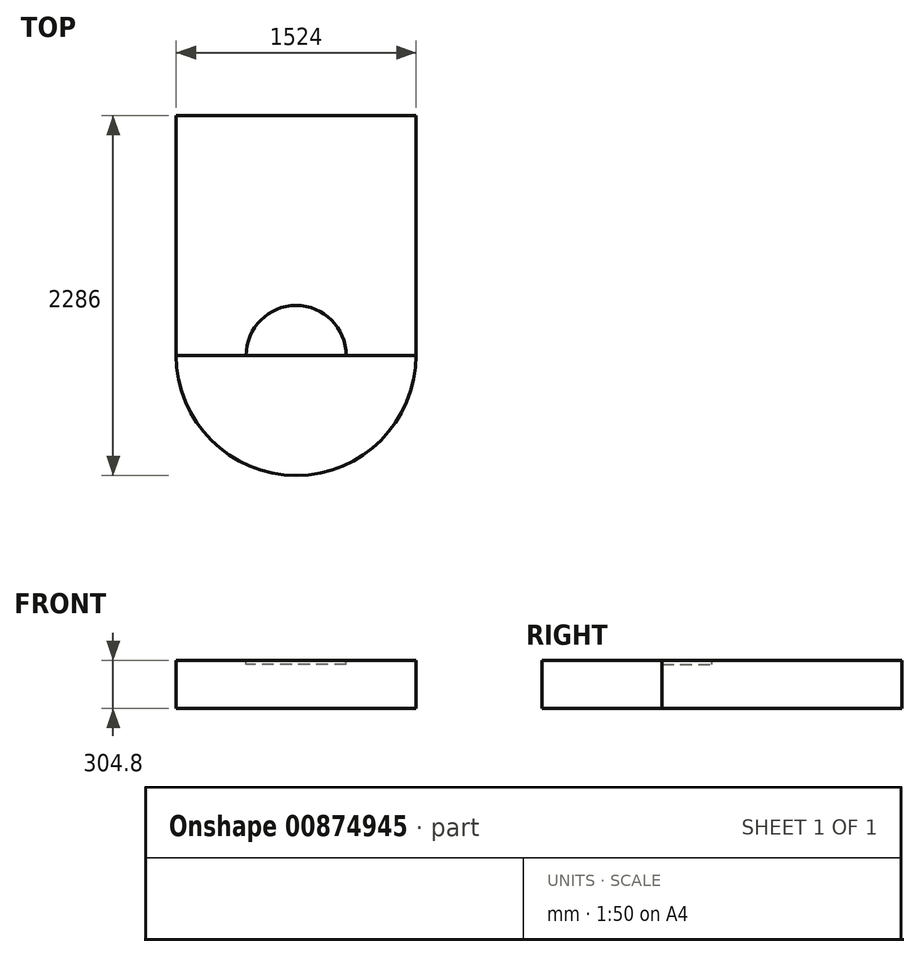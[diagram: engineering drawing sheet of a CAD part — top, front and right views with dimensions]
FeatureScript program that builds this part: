
annotation { "Feature Type Name" : "Feature", "Feature Type Description" : "" }
export const myFeature = defineFeature(function(context is Context, id is Id, definition is map)
    precondition{}
    {
        {
            var Q0;
            Q0=qCreatedBy(makeId("Top.planeOp"),FACE);
            var sketch = newSketch(context, id + "F0", { "sketchPlane" : qUnion([Q0])});
            skLineSegment(sketch, "E0", {"start": v(0, 0) * mm, "end": v(1524, 0) * mm});
            skLineSegment(sketch, "E1", {"start": v(1524, 0) * mm, "end": v(1524, -1524) * mm});
            skLineSegment(sketch, "E2", {"start": v(1524, -1524) * mm, "end": v(0, -1524) * mm});
            skLineSegment(sketch, "E3", {"start": v(0, -1524) * mm, "end": v(0, 0) * mm});
            skSolve(sketch);
        }
        {
            var Q0;
            Q0=makeQuery(id+"F0.imprint","IMPRINT",FACE,{"disambiguationData":[TD([[makeQuery(id+"F0.imprint","IMPRINT",EDGE,{"derivedFrom":sQuery(id+"F0.wireOp",EDGE,"E0")}),-1.0]])]});
            extrude(context, id + "F1", {"entities" : qUnion([Q0]), "depth" : 304.8 * mm, "offsetDistance" : 25.4 * mm});
        }
        {
            var Q0;
            Q0=makeQuery(id+"F1.opExtrude","CAP_FACE",FACE,{"disambiguationData":[OSD([sQuery(id+"F0.wireOp",EDGE,"E0"),sQuery(id+"F0.wireOp",EDGE,"E1"),sQuery(id+"F0.wireOp",EDGE,"E2"),sQuery(id+"F0.wireOp",EDGE,"E3")])],"isStart":false});
            var sketch = newSketch(context, id + "F2", { "sketchPlane" : qUnion([Q0])});
            skCircle(sketch, "E4", {"center": v(762, -1524) * mm, "radius": 762 * mm});
            skSolve(sketch);
        }
        {
            var Q0;
            {var subQ1=makeQuery(id+"F1.opExtrude","CAP_EDGE",EDGE,{"disambiguationData":[OSD([sQuery(id+"F0.wireOp",EDGE,"E2")])],"isStart":false});Q0=makeQuery(id+"F2.imprint","IMPRINT",FACE,{"disambiguationData":[TD([[makeQuery(id+"F2.imprint","IMPRINT",EDGE,{"derivedFrom":subQ1}),1.0]])]});}
            extrude(context, id + "F3", {"entities" : qUnion([Q0]), "oppositeDirection" : true, "depth" : 304.8 * mm, "offsetDistance" : 25.4 * mm});
        }
        {
            var Q0;
            Q0=makeQuery(id+"F1.opExtrude","CAP_FACE",FACE,{"disambiguationData":[OSD([sQuery(id+"F0.wireOp",EDGE,"E0"),sQuery(id+"F0.wireOp",EDGE,"E1"),sQuery(id+"F0.wireOp",EDGE,"E2"),sQuery(id+"F0.wireOp",EDGE,"E3")])],"isStart":false});
            var sketch = newSketch(context, id + "F4", { "sketchPlane" : qUnion([Q0])});
            skCircle(sketch, "E5", {"center": v(762, -1524) * mm, "radius": 317.5 * mm});
            skSolve(sketch);
        }
        {
            var Q0;
            {var subQ0=sQuery(id+"F4.wireOp",EDGE,"E5");var subQ1=makeQuery(id+"F1.opExtrude","CAP_EDGE",EDGE,{"disambiguationData":[OSD([sQuery(id+"F0.wireOp",EDGE,"E2")])],"isStart":false});var subQ2=makeQuery(id+"F4.imprint","INTERSECT",VERTEX,{"disambiguationData":[OD(0.0)],"derivedFrom":[subQ1,subQ0]});Q0=makeQuery(id+"F4.imprint","IMPRINT",FACE,{"disambiguationData":[TD([[makeQuery(id+"F4.imprint","IMPRINT",EDGE,{"disambiguationData":[TD([[subQ2,-1.0]])],"derivedFrom":subQ0}),1.0]])]});}
            extrude(context, id + "F5", {"entities" : qUnion([Q0]), "operationType" : NewBodyOperationType.REMOVE, "oppositeDirection" : true, "depth" : 25.4 * mm, "offsetDistance" : 25.4 * mm});
        }
    });
